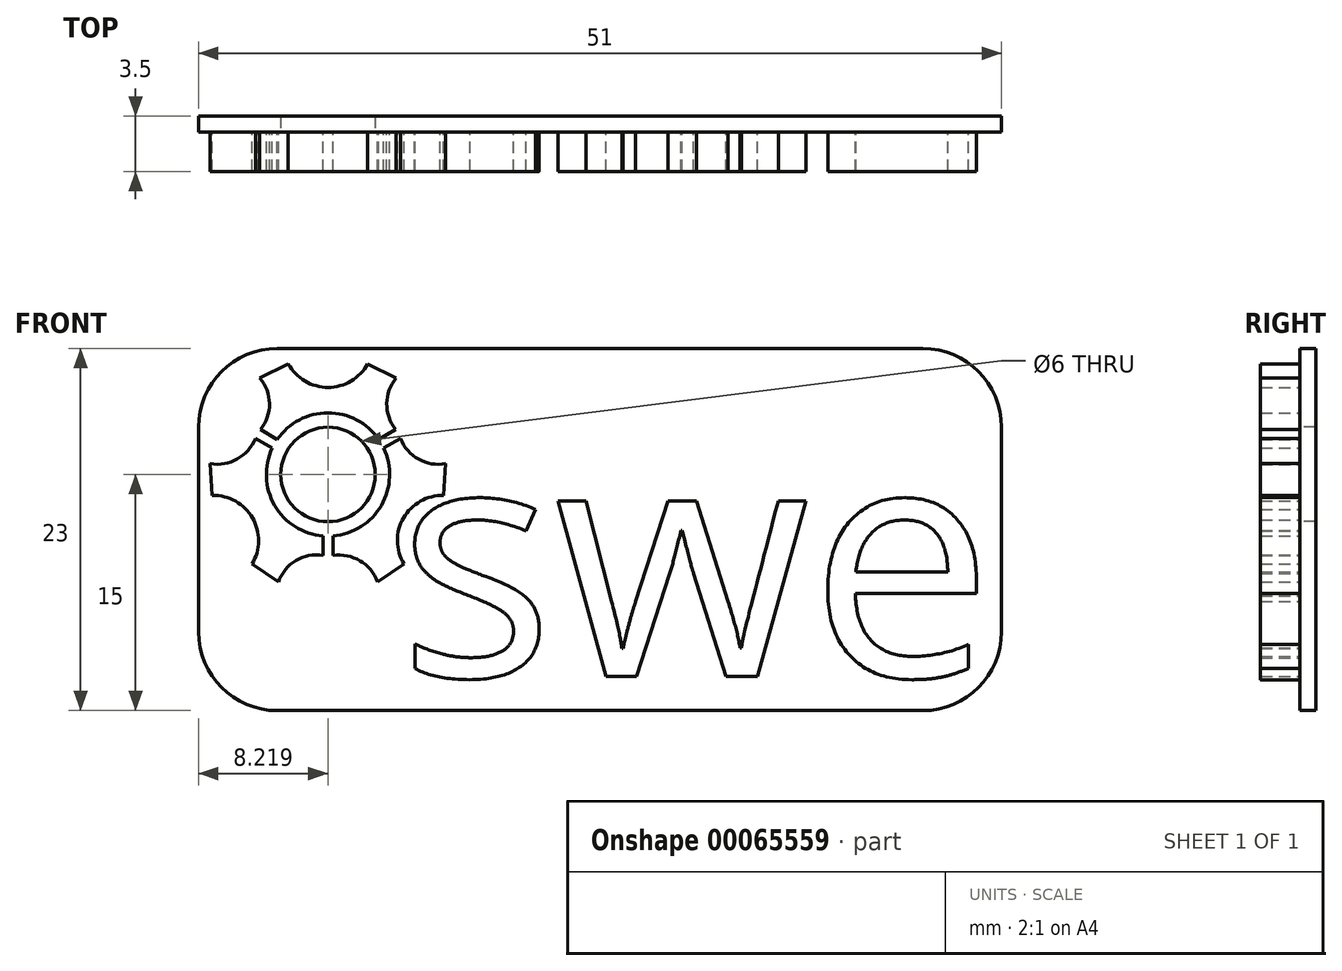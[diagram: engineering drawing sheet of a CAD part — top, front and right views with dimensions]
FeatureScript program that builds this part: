
annotation { "Feature Type Name" : "Feature", "Feature Type Description" : "" }
export const myFeature = defineFeature(function(context is Context, id is Id, definition is map)
    precondition{}
    {
        {
            var Q0;
            Q0=qCreatedBy(makeId("Front.planeOp"),FACE);
            var sketch = newSketch(context, id + "F0", { "sketchPlane" : qUnion([Q0])});
            skLineSegment(sketch, "E0.bottom", {"start": v(-23, 10) * mm, "end": v(28, 10) * mm});
            skLineSegment(sketch, "E0.top", {"start": v(-23, -13) * mm, "end": v(28, -13) * mm});
            skLineSegment(sketch, "E0.left", {"start": v(-23, 10) * mm, "end": v(-23, -13) * mm});
            skLineSegment(sketch, "E0.right", {"start": v(28, 10) * mm, "end": v(28, -13) * mm});
            skSolve(sketch);
        }
        {
            var Q0;
            Q0=makeQuery(id+"F0.imprint","IMPRINT",FACE,{"disambiguationData":[TD([[makeQuery(id+"F0.imprint","IMPRINT",EDGE,{"derivedFrom":sQuery(id+"F0.wireOp",EDGE,"E0.bottom")}),-1.0]])]});
            extrude(context, id + "F1", {"entities" : qUnion([Q0]), "oppositeDirection" : true, "depth" : 1 * mm});
        }
        {
            var Q0;
            Q0=makeQuery(id+"F1.opExtrude","CAP_FACE",FACE,{"disambiguationData":[OSD([sQuery(id+"F0.wireOp",EDGE,"E0.bottom"),sQuery(id+"F0.wireOp",EDGE,"E0.top"),sQuery(id+"F0.wireOp",EDGE,"E0.left"),sQuery(id+"F0.wireOp",EDGE,"E0.right")])],"isStart":true});
            var sketch = newSketch(context, id + "F2", { "sketchPlane" : qUnion([Q0])});
            skText(sketch, "E1", { "text": "swe", "fontName": "OpenSans-Regular.ttf"});
            const initialGuessF2  = {"E1": [-0.01035, -0.01083, 1, 0, 0.015]};
            skSetInitialGuess(sketch, initialGuessF2);
            skSolve(sketch);
        }
        {
            var Q0;
            Q0=qSketchRegion(id+"F2",true);
            extrude(context, id + "F3", {"entities" : qUnion([Q0]), "operationType" : NewBodyOperationType.ADD, "depth" : 2.5 * mm});
        }
        {
            var Q0;
            Q0=makeQuery(id+"F1.opExtrude","CAP_FACE",FACE,{"disambiguationData":[OSD([sQuery(id+"F0.wireOp",EDGE,"E0.bottom"),sQuery(id+"F0.wireOp",EDGE,"E0.top"),sQuery(id+"F0.wireOp",EDGE,"E0.left"),sQuery(id+"F0.wireOp",EDGE,"E0.right")])],"isStart":true});
            var sketch = newSketch(context, id + "F4", { "sketchPlane" : qUnion([Q0])});
            skCircle(sketch, "E2", {"center": v(-14.78, 2) * mm, "radius": 3 * mm});
            skSolve(sketch);
        }
        {
            var Q0;
            Q0=qSketchRegion(id+"F4",true);
            var Q1;
            Q1=makeQuery(id+"F1.opExtrude","CAP_FACE",FACE,{"disambiguationData":[OSD([sQuery(id+"F0.wireOp",EDGE,"E0.bottom"),sQuery(id+"F0.wireOp",EDGE,"E0.top"),sQuery(id+"F0.wireOp",EDGE,"E0.left"),sQuery(id+"F0.wireOp",EDGE,"E0.right")])],"isStart":false});
            extrude(context, id + "F5", {"entities" : qUnion([Q0]), "operationType" : NewBodyOperationType.REMOVE, "endBound" : BoundingType.UP_TO_SURFACE, "oppositeDirection" : true, "endBoundEntityFace" : qUnion([Q1]), "depth" : 25 * mm});
        }
        {
            var Q0;
            Q0=makeQuery(id+"F1.opExtrude","SWEPT_EDGE",EDGE,{"disambiguationData":[OSD([sQuery(id+"F0.wireOp",EDGE,"E0.bottom"),sQuery(id+"F0.wireOp",EDGE,"E0.left")])]});
            var Q1;
            Q1=makeQuery(id+"F1.opExtrude","SWEPT_EDGE",EDGE,{"disambiguationData":[OSD([sQuery(id+"F0.wireOp",EDGE,"E0.top"),sQuery(id+"F0.wireOp",EDGE,"E0.right")])]});
            var Q2;
            Q2=makeQuery(id+"F1.opExtrude","SWEPT_EDGE",EDGE,{"disambiguationData":[OSD([sQuery(id+"F0.wireOp",EDGE,"E0.bottom"),sQuery(id+"F0.wireOp",EDGE,"E0.right")])]});
            var Q3;
            Q3=makeQuery(id+"F1.opExtrude","SWEPT_EDGE",EDGE,{"disambiguationData":[OSD([sQuery(id+"F0.wireOp",EDGE,"E0.top"),sQuery(id+"F0.wireOp",EDGE,"E0.left")])]});
            fillet(context, id + "F6", {"entities" : qUnion([Q0, Q1, Q2, Q3]), "radius" : 5 * mm, "tangentPropagation" : true, "allowEdgeOverflow" : false});
        }
        {
            var Q0;
            {var subQ0=sQuery(id+"F0.wireOp",EDGE,"E0.top");var subQ1=sQuery(id+"F0.wireOp",EDGE,"E0.right");var subQ2=sQuery(id+"F0.wireOp",EDGE,"E0.bottom");var subQ3=sQuery(id+"F0.wireOp",EDGE,"E0.left");Q0=makeQuery(id+"F3.boolean.opBoolean","SPLIT",FACE,{"disambiguationData":[TD([makeQuery(id+"F1.opExtrude","SWEPT_FACE",FACE,{"disambiguationData":[OSD([subQ2])]})])],"derivedFrom":makeQuery(id+"F1.opExtrude","CAP_FACE",FACE,{"disambiguationData":[OSD([subQ2,subQ0,subQ3,subQ1])],"isStart":true})});}
            var sketch = newSketch(context, id + "F7", { "sketchPlane" : qUnion([Q0])});
            skPoint(sketch, "E3.centerSnap0", {"position": v(-14.78, 6.88) * mm});
            skLineSegment(sketch, "E4", {"start": v(-14.78, 13.75) * mm, "end": v(-14.78, 2) * mm, "construction": true});
            skLineSegment(sketch, "E5", {"start": v(-17.3, 9.03) * mm, "end": v(-12.26, 9.03) * mm, "construction": true});
            skLineSegment(sketch, "E6", {"start": v(-17.3, 9.03) * mm, "end": v(-19.11, 8.13) * mm, "construction": true});
            skArc(sketch, "E7", {"start": v(-17.3, 9.03) * mm, "mid": v(-14.78, 7.38) * mm, "end": v(-12.26, 9.03) * mm, "construction": true});
            skLineSegment(sketch, "E8", {"start": v(-12.26, 9.03) * mm, "end": v(-10.45, 8.13) * mm, "construction": true});
            skLineSegment(sketch, "E9", {"start": v(-10.45, 8.13) * mm, "end": v(-10.83, 6.63) * mm, "construction": true});
            skArc(sketch, "E10", {"start": v(-10.83, 6.63) * mm, "mid": v(-10.9, 5.69) * mm, "end": v(-10.5, 4.85) * mm, "construction": true});
            skLineSegment(sketch, "E11", {"start": v(-10.5, 4.85) * mm, "end": v(-11.56, 4.23) * mm, "construction": true});
            skArc(sketch, "E12", {"start": v(-11.56, 4.23) * mm, "mid": v(-14.78, 5.92) * mm, "end": v(-18, 4.23) * mm, "construction": true});
            skLineSegment(sketch, "E13", {"start": v(-19.07, 4.85) * mm, "end": v(-18, 4.23) * mm, "construction": true});
            skArc(sketch, "E14", {"start": v(-19.07, 4.85) * mm, "mid": v(-18.66, 5.69) * mm, "end": v(-18.73, 6.63) * mm, "construction": true});
            skLineSegment(sketch, "E15", {"start": v(-19.11, 8.13) * mm, "end": v(-18.73, 6.63) * mm, "construction": true});
            skLineSegment(sketch, "E16", {"start": v(-18, 4.23) * mm, "end": v(-11.56, 4.23) * mm, "construction": true});
            skLineSegment(sketch, "E17", {"start": v(-18.73, 6.63) * mm, "end": v(-10.83, 6.63) * mm, "construction": true});
            skLineSegment(sketch, "E18", {"start": v(-10.45, 8.13) * mm, "end": v(-19.11, 8.13) * mm, "construction": true});
            skLineSegment(sketch, "E19", {"start": v(-19.11, 8.13) * mm, "end": v(-17.3, 9.03) * mm});
            skLineSegment(sketch, "E20", {"start": v(-12.26, 9.03) * mm, "end": v(-10.45, 8.13) * mm});
            skLineSegment(sketch, "E21", {"start": v(-10.5, 4.85) * mm, "end": v(-11.56, 4.23) * mm});
            skLineSegment(sketch, "E22", {"start": v(-18, 4.23) * mm, "end": v(-19.07, 4.85) * mm});
            skArc(sketch, "E23", {"start": v(-17.3, 9.03) * mm, "mid": v(-14.78, 7.53) * mm, "end": v(-12.26, 9.03) * mm});
            skArc(sketch, "E24", {"start": v(-11.56, 4.23) * mm, "mid": v(-14.78, 5.92) * mm, "end": v(-18, 4.23) * mm});
            skArc(sketch, "E25", {"start": v(-10.45, 8.13) * mm, "mid": v(-11.05, 6.5) * mm, "end": v(-10.5, 4.85) * mm});
            skArc(sketch, "E26", {"start": v(-19.07, 4.85) * mm, "mid": v(-18.5, 6.5) * mm, "end": v(-19.11, 8.13) * mm});
            skArc(sketch, "E27.1.0", {"start": v(-19.6, -3.7) * mm, "mid": v(-19.57, -0.77) * mm, "end": v(-22.13, 0.67) * mm});
            skLineSegment(sketch, "E27.1.1", {"start": v(-17.93, -4.82) * mm, "end": v(-19.6, -3.7) * mm});
            skArc(sketch, "E27.1.2", {"start": v(-15.1, -3.14) * mm, "mid": v(-16.82, -3.47) * mm, "end": v(-17.93, -4.82) * mm});
            skLineSegment(sketch, "E27.1.3", {"start": v(-15.1, -1.9) * mm, "end": v(-15.1, -3.14) * mm});
            skArc(sketch, "E27.1.4", {"start": v(-18.32, 3.67) * mm, "mid": v(-18.17, 0.04) * mm, "end": v(-15.1, -1.9) * mm});
            skLineSegment(sketch, "E27.1.5", {"start": v(-19.4, 4.3) * mm, "end": v(-18.32, 3.67) * mm});
            skArc(sketch, "E27.1.6", {"start": v(-22.26, 2.69) * mm, "mid": v(-20.54, 2.98) * mm, "end": v(-19.4, 4.3) * mm});
            skLineSegment(sketch, "E27.1.7", {"start": v(-22.13, 0.67) * mm, "end": v(-22.26, 2.69) * mm});
            skArc(sketch, "E27.2.0", {"start": v(-7.44, 0.67) * mm, "mid": v(-10, -0.77) * mm, "end": v(-9.95, -3.7) * mm});
            skLineSegment(sketch, "E27.2.1", {"start": v(-7.3, 2.69) * mm, "end": v(-7.44, 0.67) * mm});
            skArc(sketch, "E27.2.2", {"start": v(-10.17, 4.3) * mm, "mid": v(-9.03, 2.97) * mm, "end": v(-7.3, 2.69) * mm});
            skLineSegment(sketch, "E27.2.3", {"start": v(-11.24, 3.67) * mm, "end": v(-10.17, 4.3) * mm});
            skArc(sketch, "E27.2.4", {"start": v(-14.46, -1.9) * mm, "mid": v(-11.4, 0.04) * mm, "end": v(-11.24, 3.67) * mm});
            skLineSegment(sketch, "E27.2.5", {"start": v(-14.46, -3.14) * mm, "end": v(-14.46, -1.9) * mm});
            skArc(sketch, "E27.2.6", {"start": v(-11.64, -4.82) * mm, "mid": v(-12.75, -3.48) * mm, "end": v(-14.46, -3.14) * mm});
            skLineSegment(sketch, "E27.2.7", {"start": v(-9.95, -3.7) * mm, "end": v(-11.64, -4.82) * mm});
            skSolve(sketch);
        }
        {
            var Q0;
            Q0 = qSketchRegion(id + "F7", true);
            extrude(context, id + "F8", {"entities" : qUnion([Q0]), "operationType" : NewBodyOperationType.ADD, "depth" : 2.5 * mm});
        }
    });
